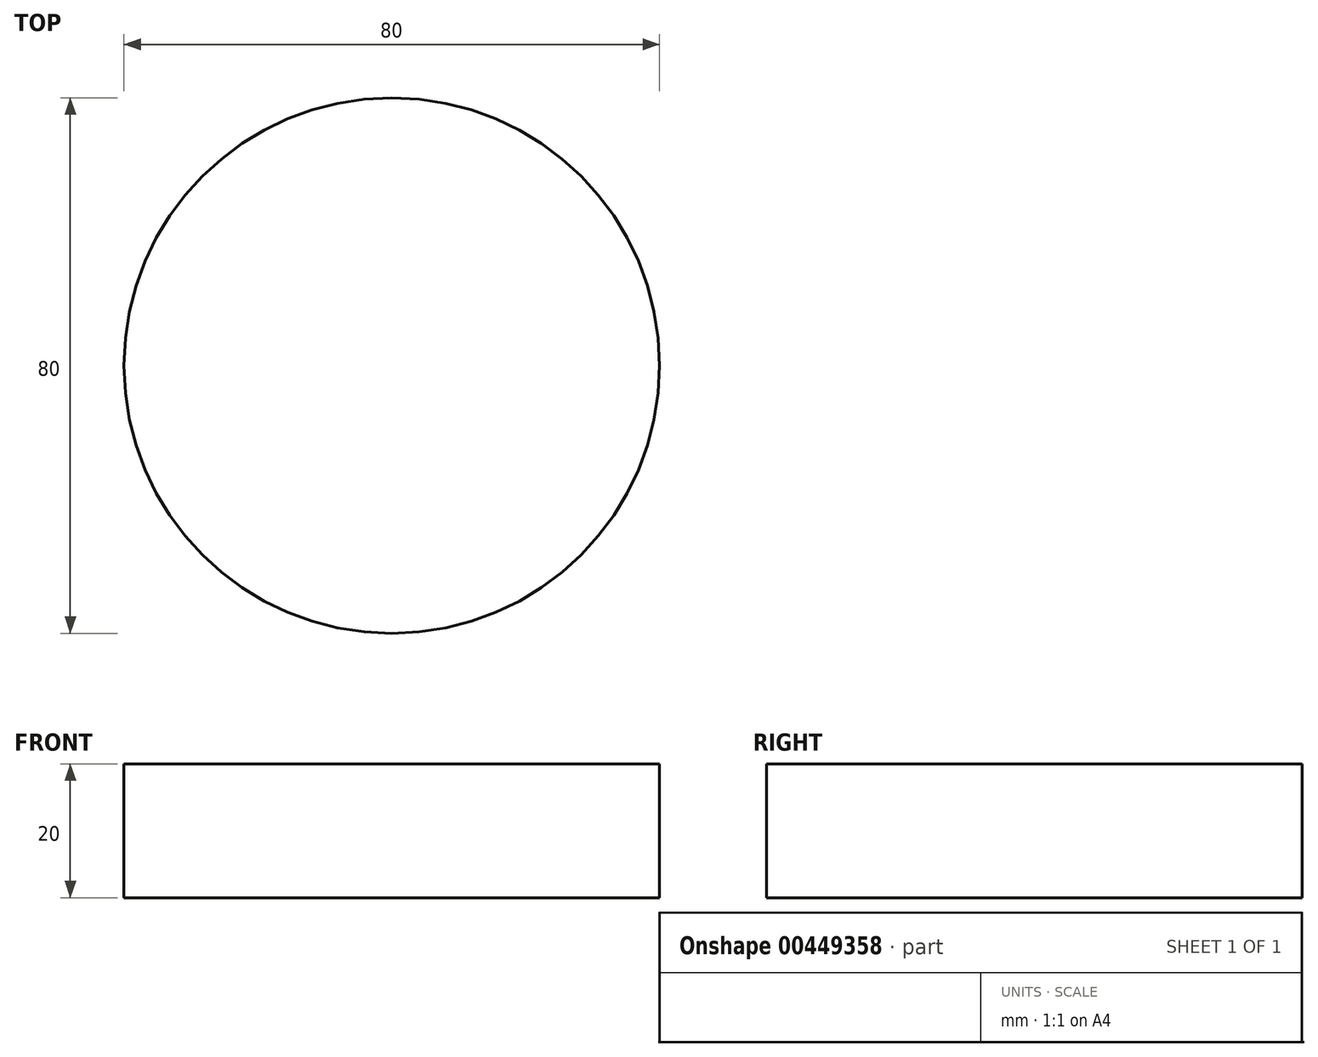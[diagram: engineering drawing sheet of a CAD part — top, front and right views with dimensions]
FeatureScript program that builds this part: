
annotation { "Feature Type Name" : "Feature", "Feature Type Description" : "" }
export const myFeature = defineFeature(function(context is Context, id is Id, definition is map)
    precondition{}
    {
        {
            var Q0;
            Q0=qCreatedBy(makeId("Front.planeOp"),FACE);
            var sketch = newSketch(context, id + "F0", { "sketchPlane" : qUnion([Q0])});
            skLineSegment(sketch, "E0.bottom", {"start": v(0, 0) * mm, "end": v(40, 0) * mm});
            skLineSegment(sketch, "E0.top", {"start": v(0, 20) * mm, "end": v(40, 20) * mm});
            skLineSegment(sketch, "E0.left", {"start": v(0, 0) * mm, "end": v(0, 20) * mm});
            skLineSegment(sketch, "E0.right", {"start": v(40, 0) * mm, "end": v(40, 20) * mm});
            skSolve(sketch);
        }
        {
            var Q0;
            Q0=makeQuery(id+"F0.imprint","IMPRINT",FACE,{"disambiguationData":[TD([[makeQuery(id+"F0.imprint","IMPRINT",EDGE,{"derivedFrom":sQuery(id+"F0.wireOp",EDGE,"E0.bottom")}),1.0]])]});
            var Q1;
            Q1=sQuery(id+"F0.wireOp",EDGE,"E0.left");
            revolve(context, id + "F1", {"entities" : qUnion([Q0]), "axis" : qUnion([Q1]), "revolveType" : RevolveType.FULL});
        }
    });
